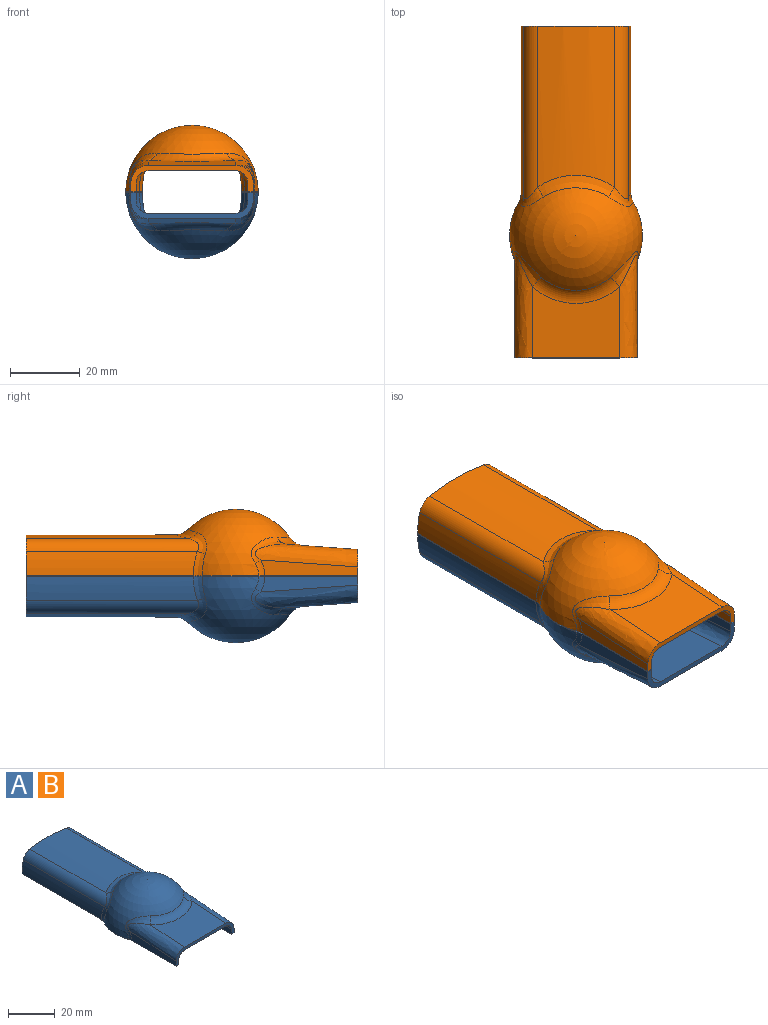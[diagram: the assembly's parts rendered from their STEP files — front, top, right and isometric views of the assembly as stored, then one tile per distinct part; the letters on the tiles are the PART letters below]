
ASSEMBLY  parts=2 mates=1
PART A: 46 faces, bbox 41x98.3x27.8 mm
  f0: plane 95.01x4.79mm, normal (0,0,-1), area 143.6mm2, adj f1,f5,f7,f9,f13,f16,f23,f25
  f1: sphere r=19mm, area 1255.5mm2, adj f0,f8,f9,f10,f11,f12,f19,f20
  f2: cylinder r=60mm len=46.12mm, axis (0,-1,0), area 966mm2, adj f3,f6,f7,f10
  f3: cylinder r=5mm len=49.48mm, axis (0,-1,0), area 280.4mm2, adj f2,f4,f7,f11
  f4: cylinder r=30mm len=49.03mm, axis (0,-1,0), area 336.2mm2, adj f3,f7,f12,f24
  f5: cylinder r=30mm len=49.03mm, axis (0,-1,0), area 336.2mm2, adj f0,f6,f7,f9
  f6: cylinder r=5mm len=49.48mm, axis (0,-1,0), area 280.4mm2, adj f2,f5,f7,f8
  f7: plane 31.43x11.66mm, normal (0,1,0), area 67.7mm2, adj f0,f2,f3,f4,f5,f6,f24,f26
  f8: bspline ~7.54x6.97mm, area 22.7mm2, adj f1,f6,f9,f10
  f9: bspline ~9.36x3.88mm, area 17.5mm2, adj f0,f1,f5,f8
  f10: bspline ~24.83x7.18mm, area 84.5mm2, adj f1,f2,f8,f11
  f11: bspline ~6.89x6.7mm, area 22.7mm2, adj f1,f3,f10,f12
  f12: bspline ~9.82x3.88mm, area 17.5mm2, adj f1,f4,f11,f24
  f13: plane 35.41x7.91mm, normal (0,-1,0), area 65.1mm2, adj f0,f14,f15,f16,f17,f18,f24,f36
  f14: bspline ~35x15.76mm, area 207.5mm2, adj f13,f15,f18,f20
  f15: plane 27.96x4.5mm, normal (-1,0,0), area 93.8mm2, adj f13,f14,f22,f24
  f16: plane 27.96x4.5mm, normal (1,0,0), area 93.8mm2, adj f0,f13,f17,f23
  f17: bspline ~35x15.76mm, area 207.5mm2, adj f13,f16,f18,f21
  f18: plane 25x20.34mm, normal (0,-0.07,1), area 428mm2, adj f13,f14,f17,f19
  f19: torus R=18.76mm, axis (0,0.07,-1), area 109mm2, adj f1,f18,f20,f21
  f20: bspline ~10.18x7.94mm, area 33.3mm2, adj f1,f14,f19,f22
  f21: bspline ~10.18x7.94mm, area 33.3mm2, adj f1,f17,f19,f23
  f22: torus R=8.35mm, axis (-1,0,0), area 7.6mm2, adj f1,f15,f20,f24
  f23: torus R=8.35mm, axis (-1,0,0), area 7.6mm2, adj f0,f1,f16,f21
  f24: plane 95.01x4.79mm, normal (0,0,-1), area 143.6mm2, adj f1,f4,f7,f12,f13,f15,f22,f25
  f25: sphere r=17.5mm, area 1065.1mm2, adj f0,f24,f31,f32,f33,f34,f35,f41
  f26: cylinder r=58.5mm len=46.12mm, axis (0,-1,0), area 941.8mm2, adj f7,f27,f30,f33
  f27: cylinder r=3.5mm len=49.48mm, axis (0,-1,0), area 196.3mm2, adj f7,f26,f28,f34
  f28: cylinder r=28.5mm len=49.03mm, axis (0,-1,0), area 319.4mm2, adj f7,f24,f27,f35
  f29: cylinder r=28.5mm len=49.03mm, axis (0,-1,0), area 319.4mm2, adj f0,f7,f30,f32
  f30: cylinder r=3.5mm len=49.48mm, axis (0,-1,0), area 196.3mm2, adj f7,f26,f29,f31
  f31: bspline ~6.45x6.35mm, area 25.2mm2, adj f25,f30,f32,f33
  f32: bspline ~8.89x4.53mm, area 21.3mm2, adj f0,f25,f29,f31
  f33: bspline ~24.2x7.98mm, area 104.2mm2, adj f25,f26,f31,f34
  f34: bspline ~7.14x6.95mm, area 25.2mm2, adj f25,f27,f33,f35
  f35: bspline ~9.33x4.53mm, area 21.3mm2, adj f24,f25,f28,f34
  f36: offset ~38.35x18.76mm, area 145.5mm2, adj f13,f37,f40,f42
  f37: plane 27.96x4.5mm, normal (1,0,0), area 93.8mm2, adj f13,f24,f36,f44
  f38: plane 27.96x4.5mm, normal (-1,0,0), area 93.8mm2, adj f0,f13,f39,f45
  f39: offset ~38.35x18.76mm, area 145.5mm2, adj f13,f38,f40,f43
  f40: plane 25x20.45mm, normal (0,0.07,-1), area 430.7mm2, adj f13,f36,f39,f41
  f41: torus R=18.76mm, axis (0,0.07,-1), area 136.4mm2, adj f25,f40,f42,f43
  f42: bspline ~10.5x7.36mm, area 38.6mm2, adj f25,f36,f41,f44
  f43: bspline ~10.5x7.36mm, area 38.6mm2, adj f25,f39,f41,f45
  f44: torus R=8.35mm, axis (-1,0,0), area 9.5mm2, adj f24,f25,f37,f42
  f45: torus R=8.35mm, axis (-1,0,0), area 9.5mm2, adj f0,f25,f38,f43
PART B: same geometry as A
PLACE A rot(axis=(0,1,0),180deg) t=(-26.38,-38.13,-8.16)mm
PLACE B rot(axis=(0,-1,0),0deg) t=(-26.38,-38.13,-7.96)mm
MATE cylindrical B.f0 <-> A.f24  axis (0,0,1) through (-8.57,-44.74,-7.96)mm
